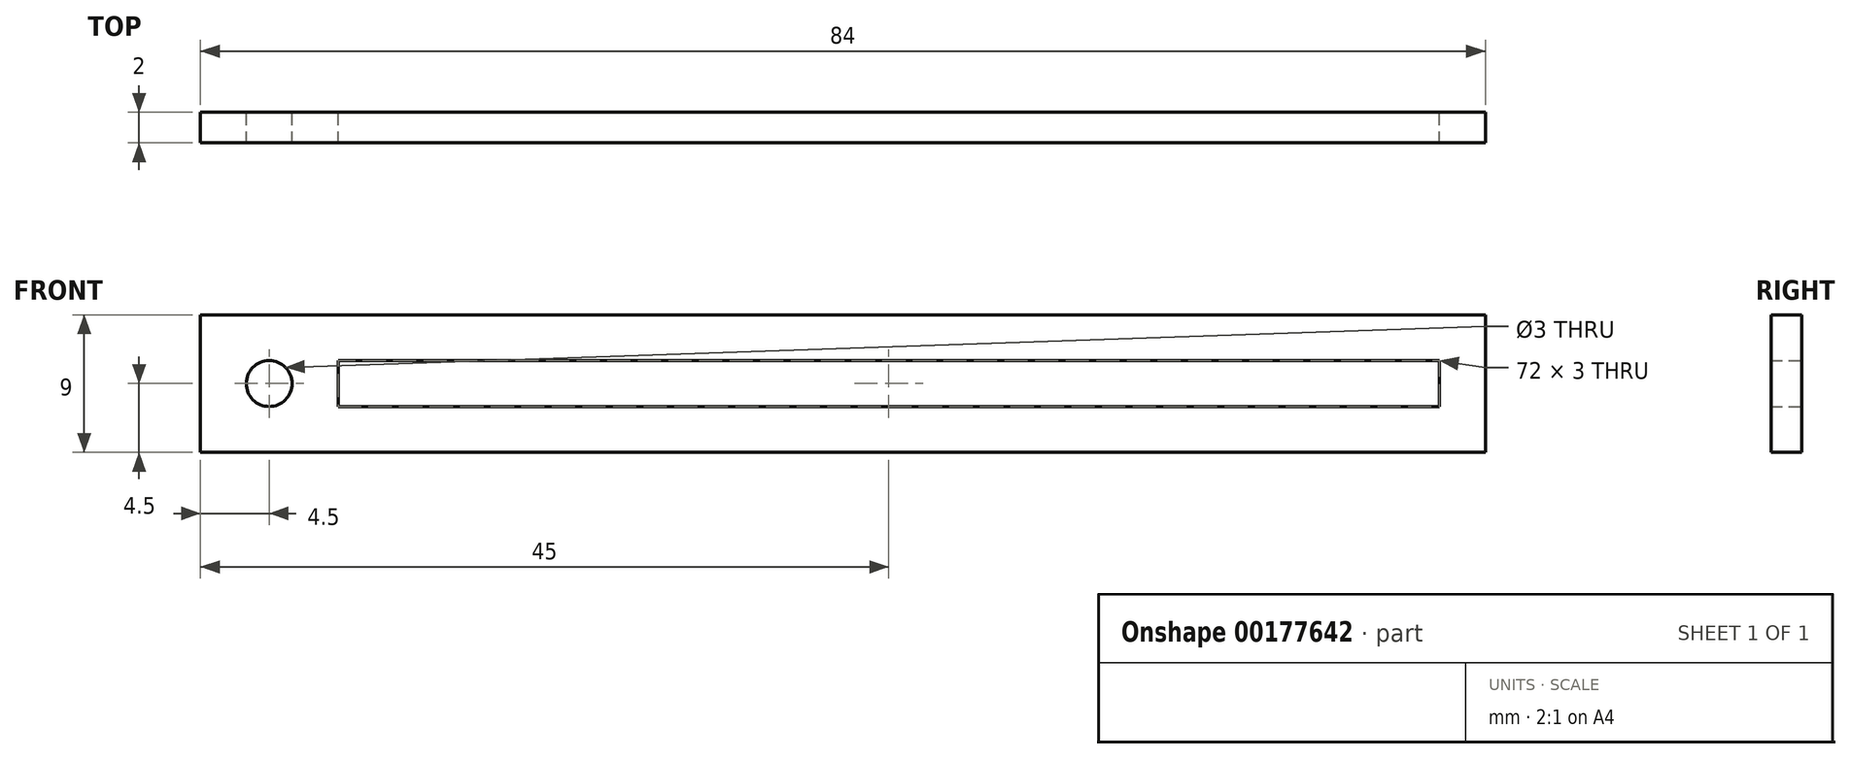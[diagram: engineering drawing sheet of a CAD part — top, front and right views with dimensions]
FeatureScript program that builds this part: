
annotation { "Feature Type Name" : "Feature", "Feature Type Description" : "" }
export const myFeature = defineFeature(function(context is Context, id is Id, definition is map)
    precondition{}
    {
        {
            var Q0;
            Q0=qCreatedBy(makeId("Front.planeOp"),FACE);
            var sketch = newSketch(context, id + "F0", { "sketchPlane" : qUnion([Q0])});
            skLineSegment(sketch, "E0.bottom", {"start": v(42, 4.5) * mm, "end": v(-42, 4.5) * mm});
            skLineSegment(sketch, "E0.top", {"start": v(42, -4.5) * mm, "end": v(-42, -4.5) * mm});
            skLineSegment(sketch, "E0.left", {"start": v(42, 4.5) * mm, "end": v(42, -4.5) * mm});
            skLineSegment(sketch, "E0.right", {"start": v(-42, 4.5) * mm, "end": v(-42, -4.5) * mm});
            skPoint(sketch, "E0.middle", {"position": v(0, 0) * mm});
            skLineSegment(sketch, "E1.bottom", {"start": v(39, 1.5) * mm, "end": v(-33, 1.5) * mm});
            skLineSegment(sketch, "E1.top", {"start": v(39, -1.5) * mm, "end": v(-33, -1.5) * mm});
            skLineSegment(sketch, "E1.left", {"start": v(39, 1.5) * mm, "end": v(39, -1.5) * mm});
            skLineSegment(sketch, "E1.right", {"start": v(-33, 1.5) * mm, "end": v(-33, -1.5) * mm});
            skCircle(sketch, "E2", {"center": v(-37.5, 0) * mm, "radius": 1.5 * mm});
            skSolve(sketch);
        }
        {
            var Q0;
            Q0 = qSketchRegion(id + "F0", true);
            extrude(context, id + "F1", {"entities" : qUnion([Q0]), "depth" : 2 * mm});
        }
    });
